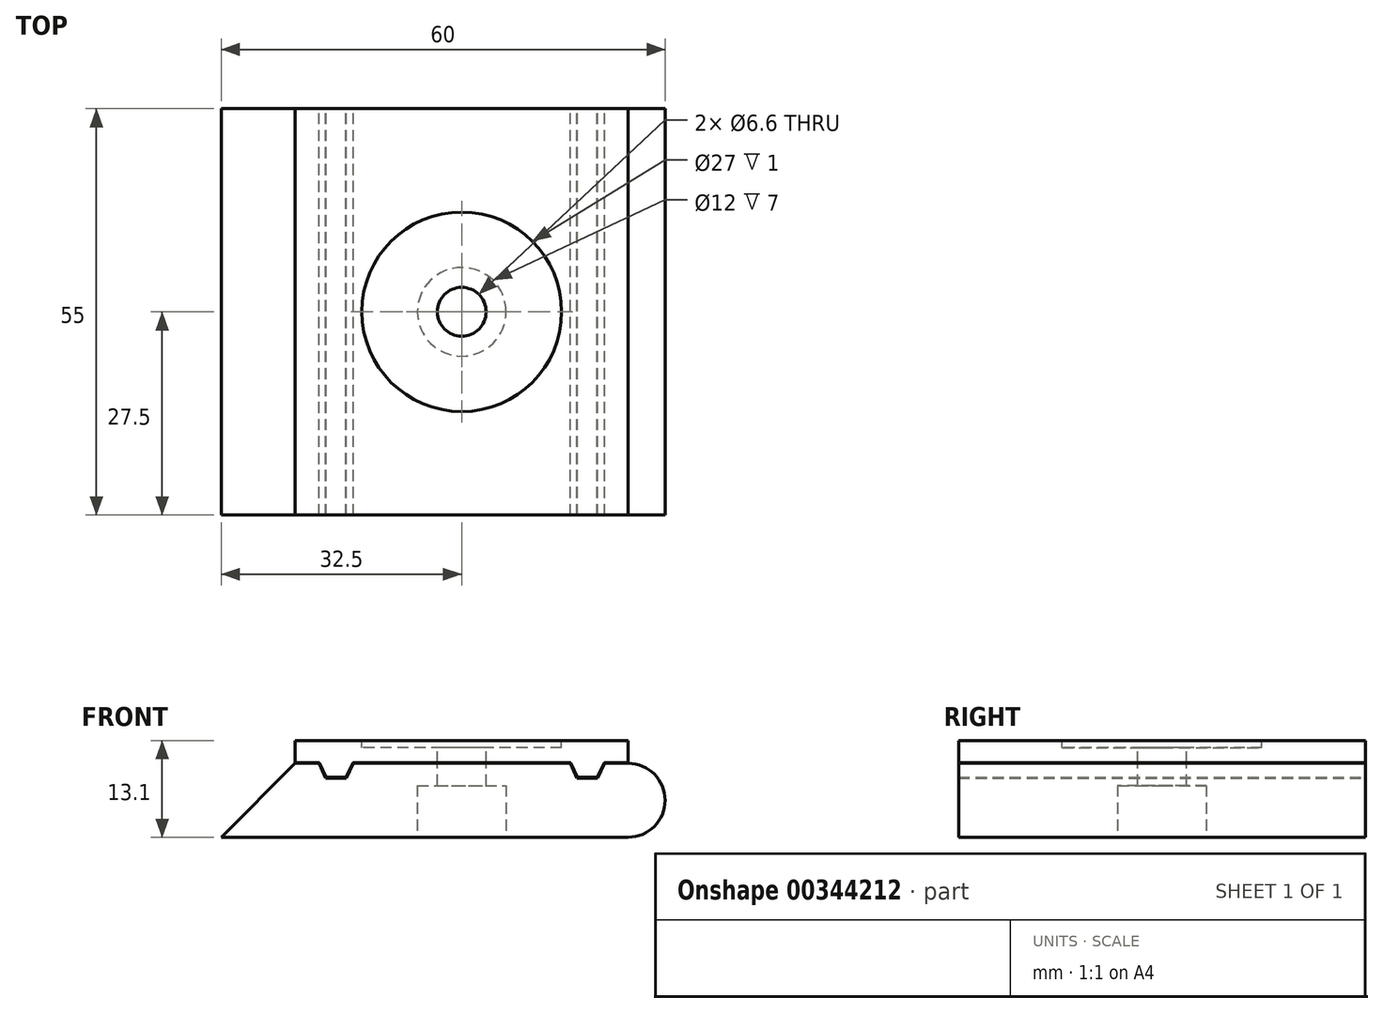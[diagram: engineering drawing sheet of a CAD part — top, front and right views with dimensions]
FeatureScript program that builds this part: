
annotation { "Feature Type Name" : "Feature", "Feature Type Description" : "" }
export const myFeature = defineFeature(function(context is Context, id is Id, definition is map)
    precondition{}
    {
        {
            var Q0;
            Q0=qCreatedBy(makeId("Front.planeOp"),FACE);
            var sketch = newSketch(context, id + "F0", { "sketchPlane" : qUnion([Q0])});
            skLineSegment(sketch, "E0.bottom", {"start": v(27.5, -5) * mm, "end": v(-27.5, -5) * mm});
            skLineSegment(sketch, "E0.top", {"start": v(27.5, 5) * mm, "end": v(24.31, 5) * mm});
            skPoint(sketch, "E0.middle", {"position": v(0, 0) * mm});
            skLineSegment(sketch, "E1", {"start": v(-27.5, -5) * mm, "end": v(-17.5, 5) * mm});
            skPoint(sketch, "E0.right.end.orphan", {"position": v(-27.5, 5) * mm});
            skArc(sketch, "E2", {"start": v(27.5, -5) * mm, "mid": v(32.5, 0) * mm, "end": v(27.5, 5) * mm});
            skLineSegment(sketch, "E3", {"start": v(5, 5) * mm, "end": v(5, 15.34) * mm, "construction": true});
            skLineSegment(sketch, "E4", {"start": v(5, 15.34) * mm, "end": v(5, -9.4) * mm, "construction": true});
            skLineSegment(sketch, "E5", {"start": v(24.31, 5) * mm, "end": v(23.38, 3) * mm});
            skLineSegment(sketch, "E6", {"start": v(23.38, 3) * mm, "end": v(20.58, 3) * mm});
            skLineSegment(sketch, "E7", {"start": v(20.58, 3) * mm, "end": v(19.65, 5) * mm});
            skLineSegment(sketch, "E8.trimOffspring", {"start": v(19.65, 5) * mm, "end": v(-9.65, 5) * mm});
            skLineSegment(sketch, "E9.MirrorCS", {"start": v(-14.31, 5) * mm, "end": v(-13.38, 3) * mm});
            skLineSegment(sketch, "E10.MirrorCS", {"start": v(-13.38, 3) * mm, "end": v(-10.58, 3) * mm});
            skLineSegment(sketch, "E11.MirrorCS", {"start": v(-10.58, 3) * mm, "end": v(-9.65, 5) * mm});
            skLineSegment(sketch, "E12.trimOffspring", {"start": v(-14.31, 5) * mm, "end": v(-17.5, 5) * mm});
            skSolve(sketch);
        }
        {
            var Q0;
            Q0 = qSketchRegion(id + "F0", true);
            extrude(context, id + "F1", {"entities" : qUnion([Q0]), "depth" : 55 * mm});
        }
        {
            var Q0;
            Q0=qCreatedBy(makeId("Front.planeOp"),FACE);
            var sketch = newSketch(context, id + "F2", { "sketchPlane" : qUnion([Q0])});
            skPoint(sketch, "E13.0", {"position": v(27.5, 5) * mm});
            skLineSegment(sketch, "E14.0", {"start": v(24.22, 5.04) * mm, "end": v(23.32, 3.1) * mm});
            skLineSegment(sketch, "E15.0", {"start": v(23.32, 3.1) * mm, "end": v(20.65, 3.1) * mm});
            skLineSegment(sketch, "E16.0", {"start": v(20.65, 3.1) * mm, "end": v(19.74, 5.04) * mm});
            skLineSegment(sketch, "E17.0", {"start": v(19.65, 5.1) * mm, "end": v(-9.65, 5.1) * mm});
            skArc(sketch, "E18", {"start": v(19.74, 5.04) * mm, "mid": v(19.7, 5.08) * mm, "end": v(19.65, 5.1) * mm});
            skLineSegment(sketch, "E19.0", {"start": v(27.5, 5.1) * mm, "end": v(24.31, 5.1) * mm});
            skLineSegment(sketch, "E20.0", {"start": v(-10.65, 3.1) * mm, "end": v(-9.74, 5.04) * mm});
            skLineSegment(sketch, "E21.0", {"start": v(-13.32, 3.1) * mm, "end": v(-10.65, 3.1) * mm});
            skLineSegment(sketch, "E22.0", {"start": v(-14.22, 5.04) * mm, "end": v(-13.32, 3.1) * mm});
            skLineSegment(sketch, "E23.0", {"start": v(-14.31, 5.1) * mm, "end": v(-17.5, 5.1) * mm});
            skArc(sketch, "E24", {"start": v(-9.65, 5.1) * mm, "mid": v(-9.7, 5.08) * mm, "end": v(-9.74, 5.04) * mm});
            skArc(sketch, "E25", {"start": v(-14.22, 5.04) * mm, "mid": v(-14.26, 5.08) * mm, "end": v(-14.31, 5.1) * mm});
            skPoint(sketch, "E26.0.start.orphan", {"position": v(24.31, 5) * mm});
            skArc(sketch, "E27", {"start": v(24.31, 5.1) * mm, "mid": v(24.26, 5.08) * mm, "end": v(24.22, 5.04) * mm});
            skPoint(sketch, "E28.0.start.orphan", {"position": v(23.38, 3) * mm});
            skPoint(sketch, "E29.0.start.orphan", {"position": v(20.58, 3) * mm});
            skPoint(sketch, "E30.0.end.orphan", {"position": v(-10.58, 3) * mm});
            skPoint(sketch, "E31.0.end.orphan", {"position": v(-13.38, 3) * mm});
            skPoint(sketch, "E32.0.end.orphan", {"position": v(-17.5, 5) * mm});
            skLineSegment(sketch, "E33.top", {"start": v(27.5, 8.1) * mm, "end": v(-17.5, 8.1) * mm});
            skLineSegment(sketch, "E33.left", {"start": v(27.5, 5.1) * mm, "end": v(27.5, 8.1) * mm});
            skLineSegment(sketch, "E33.right", {"start": v(-17.5, 5.1) * mm, "end": v(-17.5, 8.1) * mm});
            skSolve(sketch);
        }
        {
            var Q0;
            Q0 = qSketchRegion(id + "F2", true);
            extrude(context, id + "F3", {"entities" : qUnion([Q0]), "depth" : 55 * mm});
        }
        {
            var Q0;
            Q0=makeQuery(id+"F3.opExtrude","SWEPT_FACE",FACE,{"disambiguationData":[OSD([sQuery(id+"F2.wireOp",EDGE,"E33.top")])]});
            var sketch = newSketch(context, id + "F4", { "sketchPlane" : qUnion([Q0])});
            skLineSegment(sketch, "E34", {"start": v(27.5, -55) * mm, "end": v(-17.5, 0) * mm, "construction": true});
            skLineSegment(sketch, "E35", {"start": v(-17.5, 0) * mm, "end": v(-17.5, -55) * mm, "construction": true});
            skLineSegment(sketch, "E36", {"start": v(-17.5, -55) * mm, "end": v(27.5, 0) * mm, "construction": true});
            skCircle(sketch, "E37", {"center": v(5, -27.5) * mm, "radius": 13.5 * mm});
            skSolve(sketch);
        }
        {
            var Q0;
            Q0 = qSketchRegion(id + "F4", true);
            extrude(context, id + "F5", {"entities" : qUnion([Q0]), "operationType" : NewBodyOperationType.REMOVE, "oppositeDirection" : true, "depth" : 1 * mm});
        }
        {
            var Q0;
            Q0=makeQuery(id+"F5.boolean.opBoolean","COPY",FACE,{"derivedFrom":makeQuery(id+"F5.opExtrude","CAP_FACE",FACE,{"disambiguationData":[OSD([sQuery(id+"F4.wireOp",EDGE,"E37")])],"isStart":false})});
            var sketch = newSketch(context, id + "F6", { "sketchPlane" : qUnion([Q0])});
            skCircle(sketch, "E38", {"center": v(5, -27.5) * mm, "radius": 3.3 * mm});
            skSolve(sketch);
        }
        {
            var Q0;
            Q0 = qSketchRegion(id + "F6", true);
            extrude(context, id + "F7", {"entities" : qUnion([Q0]), "operationType" : NewBodyOperationType.REMOVE, "endBound" : BoundingType.THROUGH_ALL, "oppositeDirection" : true, "depth" : 25 * mm});
        }
        {
            var Q0;
            Q0=makeQuery(id+"F1.opExtrude","SWEPT_FACE",FACE,{"disambiguationData":[OSD([sQuery(id+"F0.wireOp",EDGE,"E8.trimOffspring")])]});
            var sketch = newSketch(context, id + "F8", { "sketchPlane" : qUnion([Q0])});
            skCircle(sketch, "E39.0", {"center": v(5, -27.5) * mm, "radius": 3.3 * mm});
            skSolve(sketch);
        }
        {
            var Q0;
            Q0 = qSketchRegion(id + "F8", true);
            extrude(context, id + "F9", {"entities" : qUnion([Q0]), "operationType" : NewBodyOperationType.REMOVE, "oppositeDirection" : true, "depth" : 25 * mm});
        }
        {
            var Q0;
            Q0=makeQuery(id+"F1.opExtrude","SWEPT_FACE",FACE,{"disambiguationData":[OSD([sQuery(id+"F0.wireOp",EDGE,"E0.bottom")])]});
            var sketch = newSketch(context, id + "F10", { "sketchPlane" : qUnion([Q0])});
            skCircle(sketch, "E40", {"center": v(5, 27.5) * mm, "radius": 6 * mm});
            skSolve(sketch);
        }
        {
            var Q0;
            Q0 = qSketchRegion(id + "F10", true);
            extrude(context, id + "F11", {"entities" : qUnion([Q0]), "operationType" : NewBodyOperationType.REMOVE, "oppositeDirection" : true, "depth" : 7 * mm});
        }
    });
